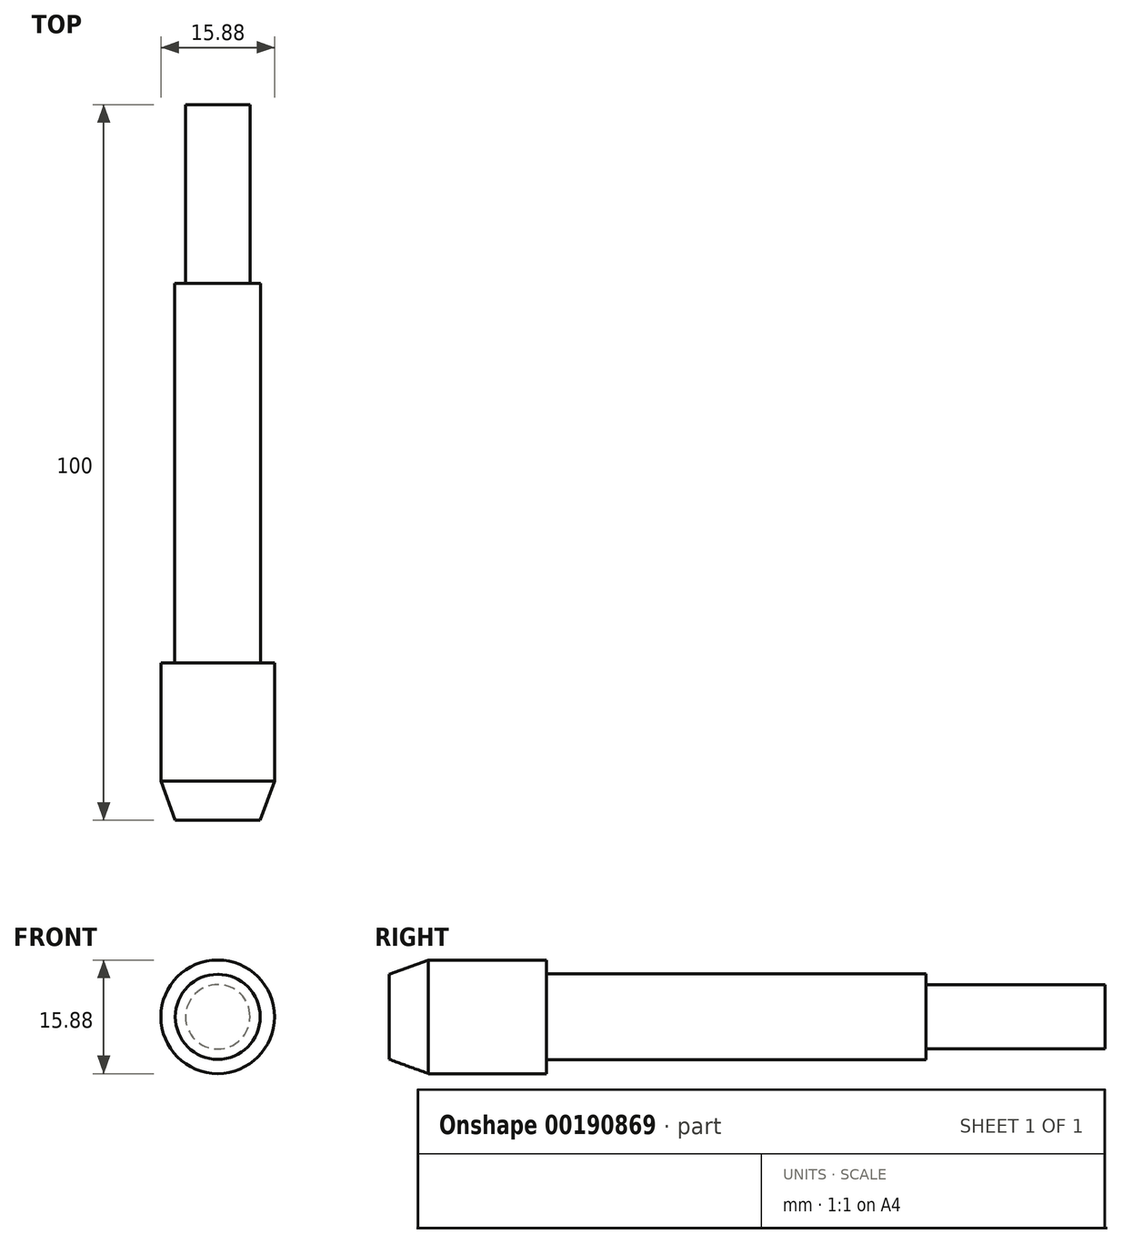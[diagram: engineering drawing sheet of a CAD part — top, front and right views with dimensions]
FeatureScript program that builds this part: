
annotation { "Feature Type Name" : "Feature", "Feature Type Description" : "" }
export const myFeature = defineFeature(function(context is Context, id is Id, definition is map)
    precondition{}
    {
        {
            var Q0;
            Q0=qCreatedBy(makeId("Front.planeOp"),FACE);
            var sketch = newSketch(context, id + "F0", { "sketchPlane" : qUnion([Q0])});
            skCircle(sketch, "E0", {"center": v(0, 0) * mm, "radius": 7.94 * mm});
            skSolve(sketch);
        }
        {
            var Q0;
            Q0 = qSketchRegion(id + "F0", true);
            extrude(context, id + "F1", {"entities" : qUnion([Q0]), "depth" : 22 * mm});
        }
        {
            var Q0;
            Q0=qCreatedBy(makeId("Front.planeOp"),FACE);
            var sketch = newSketch(context, id + "F2", { "sketchPlane" : qUnion([Q0])});
            skCircle(sketch, "E1", {"center": v(0, 0) * mm, "radius": 6 * mm});
            skSolve(sketch);
        }
        {
            var Q0;
            Q0=makeQuery(id+"F2.imprint","IMPRINT",FACE,{"disambiguationData":[TD([[makeQuery(id+"F2.imprint","IMPRINT",EDGE,{"derivedFrom":sQuery(id+"F2.wireOp",EDGE,"E1")}),1.0]])]});
            var Q1;
            Q1 = qSketchRegion(id + "FCUHNVKQJGT64kM_1", true);
            extrude(context, id + "F3", {"entities" : qUnion([Q0, Q1]), "operationType" : NewBodyOperationType.ADD, "oppositeDirection" : true, "depth" : 78 * mm});
        }
        {
            var Q0;
            Q0=makeQuery(id+"F3.opExtrude","CAP_FACE",FACE,{"disambiguationData":[OSD([sQuery(id+"F2.wireOp",EDGE,"E1")])],"isStart":false});
            var sketch = newSketch(context, id + "F4", { "sketchPlane" : qUnion([Q0])});
            skCircle(sketch, "E2", {"center": v(0, 0) * mm, "radius": 4.5 * mm});
            skSolve(sketch);
        }
        {
            var Q0;
            Q0=makeQuery(id+"F4.imprint","IMPRINT",FACE,{"disambiguationData":[TD([[makeQuery(id+"F4.imprint","IMPRINT",EDGE,{"derivedFrom":sQuery(id+"F4.wireOp",EDGE,"E2")}),-1.0]])]});
            extrude(context, id + "F5", {"entities" : qUnion([Q0]), "operationType" : NewBodyOperationType.REMOVE, "oppositeDirection" : true, "depth" : 25 * mm});
        }
        {
            var Q0;
            Q0=makeQuery(id+"F1.opExtrude","CAP_EDGE",EDGE,{"disambiguationData":[OSD([sQuery(id+"F0.wireOp",EDGE,"E0")])],"isStart":false});
            chamfer(context, id + "F6", {"entities" : qUnion([Q0]), "chamferType" : ChamferType.OFFSET_ANGLE, "width" : 2 * mm, "oppositeDirection" : false, "angle" : 70 * degree, "tangentPropagation" : true});
        }
    });
